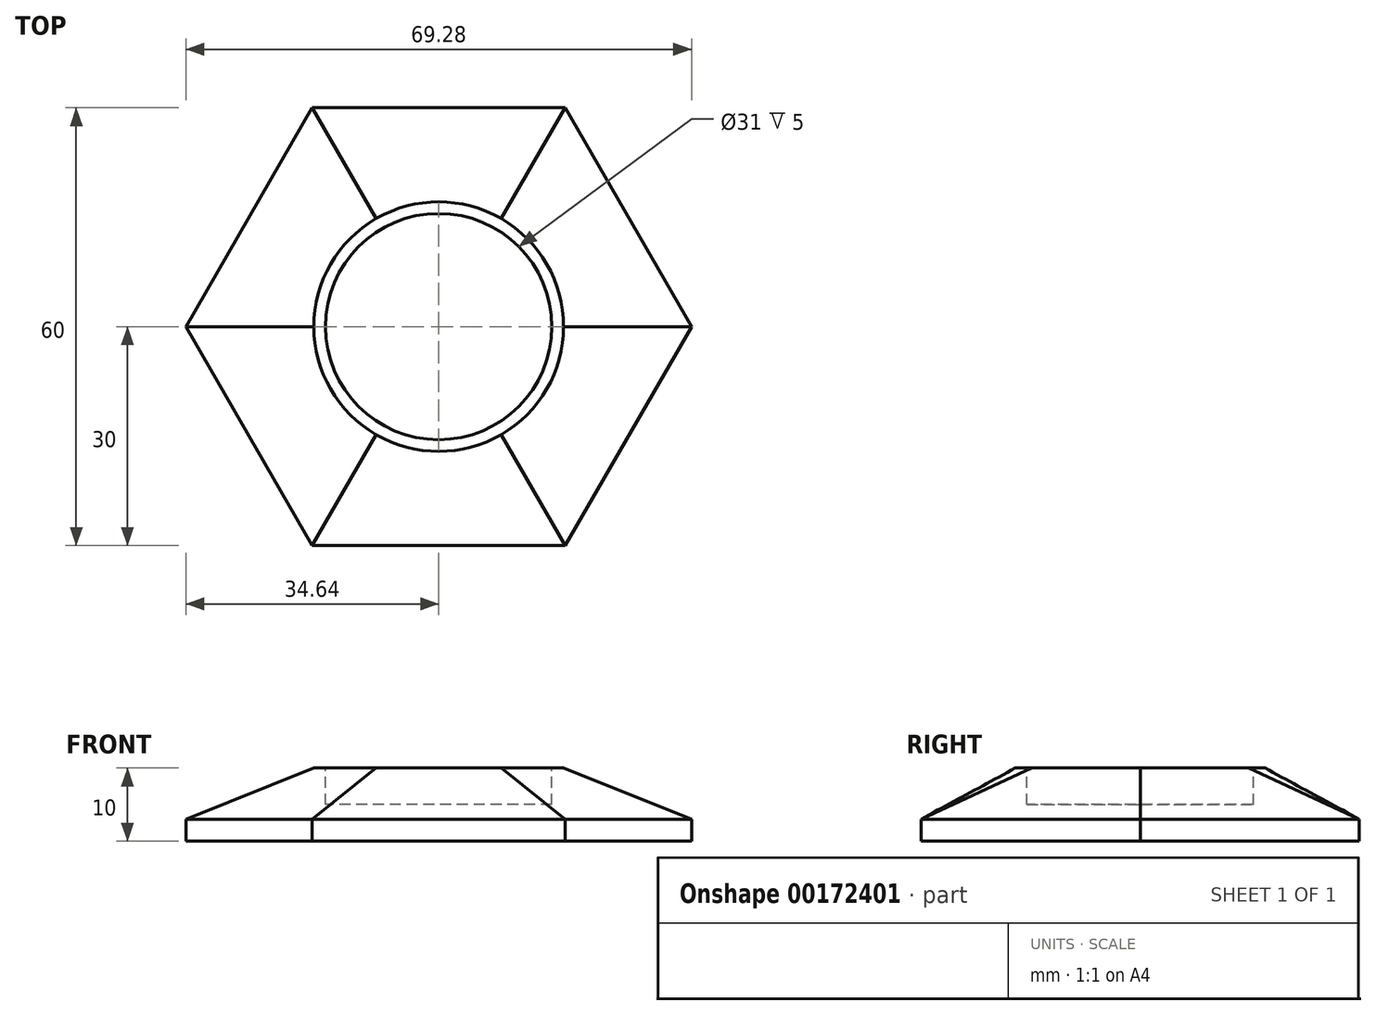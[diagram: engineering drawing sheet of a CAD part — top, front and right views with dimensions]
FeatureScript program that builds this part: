
annotation { "Feature Type Name" : "Feature", "Feature Type Description" : "" }
export const myFeature = defineFeature(function(context is Context, id is Id, definition is map)
    precondition{}
    {
        {
            var Q0;
            Q0=qCreatedBy(makeId("Top.planeOp"),FACE);
            var sketch = newSketch(context, id + "F0", { "sketchPlane" : qUnion([Q0])});
            skCircle(sketch, "E0.cCircle", {"center": v(0, 0) * mm, "radius": 30 * mm, "construction": true});
            skLineSegment(sketch, "E0.0", {"start": v(-17.32, 30) * mm, "end": v(17.32, 30) * mm});
            skLineSegment(sketch, "E0.1", {"start": v(17.32, 30) * mm, "end": v(34.64, 0) * mm});
            skLineSegment(sketch, "E0.2", {"start": v(34.64, 0) * mm, "end": v(17.32, -30) * mm});
            skLineSegment(sketch, "E0.3", {"start": v(17.32, -30) * mm, "end": v(-17.32, -30) * mm});
            skLineSegment(sketch, "E0.4", {"start": v(-17.32, -30) * mm, "end": v(-34.64, 0) * mm});
            skLineSegment(sketch, "E0.5", {"start": v(-34.64, 0) * mm, "end": v(-17.32, 30) * mm});
            skPoint(sketch, "E0.0.midPoint", {"position": v(0, 30) * mm});
            skSolve(sketch);
        }
        {
            var Q0;
            Q0=makeQuery(id+"F0.imprint","IMPRINT",FACE,{"disambiguationData":[TD([[makeQuery(id+"F0.imprint","IMPRINT",EDGE,{"derivedFrom":sQuery(id+"F0.wireOp",EDGE,"E0.0")}),-1.0]])]});
            extrude(context, id + "F1", {"entities" : qUnion([Q0]), "depth" : 3 * mm});
        }
        {
            var Q0;
            Q0=qCreatedBy(makeId("Top.planeOp"),FACE);
            cPlane(context, id + "F2", {"entities" : qUnion([Q0]), "cplaneType" : CPlaneType.OFFSET, "offset" : 10 * mm, "width" : 150 * mm, "height" : 150 * mm});
        }
        {
            var Q0;
            Q0=qCreatedBy(id+"F2.planeOp",FACE);
            var sketch = newSketch(context, id + "F3", { "sketchPlane" : qUnion([Q0])});
            skCircle(sketch, "E1", {"center": v(0, 0) * mm, "radius": 17.1 * mm});
            skSolve(sketch);
        }
        {
            var Q1;
            Q1=makeQuery(id+"F1.opExtrude","CAP_FACE",FACE,{"disambiguationData":[OSD([sQuery(id+"F0.wireOp",EDGE,"E0.0"),sQuery(id+"F0.wireOp",EDGE,"E0.1"),sQuery(id+"F0.wireOp",EDGE,"E0.2"),sQuery(id+"F0.wireOp",EDGE,"E0.3"),sQuery(id+"F0.wireOp",EDGE,"E0.4"),sQuery(id+"F0.wireOp",EDGE,"E0.5")])],"isStart":false});
            var Q2;
            Q2=makeQuery(id+"F3.imprint","IMPRINT",FACE,{"disambiguationData":[TD([[makeQuery(id+"F3.imprint","IMPRINT",EDGE,{"derivedFrom":sQuery(id+"F3.wireOp",EDGE,"E1")}),1.0]])]});
            loft(context, id + "F4", {"operationType" : NewBodyOperationType.ADD, "sheetProfilesArray" : [{ "sheetProfileEntities" : qUnion([Q1]) }, { "sheetProfileEntities" : qUnion([Q2]) }]});
        }
        {
            var Q0;
            Q0=makeQuery(id+"F4.opLoft","CAP_FACE",FACE,{"disambiguationData":[OSD([makeQuery(id+"F3.imprint","IMPRINT",FACE,{"disambiguationData":[TD([[makeQuery(id+"F3.imprint","IMPRINT",EDGE,{"derivedFrom":sQuery(id+"F3.wireOp",EDGE,"E1")}),1.0]])]})])],"isStart":true});
            var sketch = newSketch(context, id + "F5", { "sketchPlane" : qUnion([Q0])});
            skCircle(sketch, "E2", {"center": v(0, 0) * mm, "radius": 15.5 * mm});
            skSolve(sketch);
        }
        {
            var Q0;
            Q0=makeQuery(id+"F5.imprint","IMPRINT",FACE,{"disambiguationData":[TD([[makeQuery(id+"F5.imprint","IMPRINT",EDGE,{"derivedFrom":sQuery(id+"F5.wireOp",EDGE,"E2")}),1.0]])]});
            extrude(context, id + "F6", {"entities" : qUnion([Q0]), "operationType" : NewBodyOperationType.REMOVE, "oppositeDirection" : true, "depth" : 5 * mm});
        }
    });
